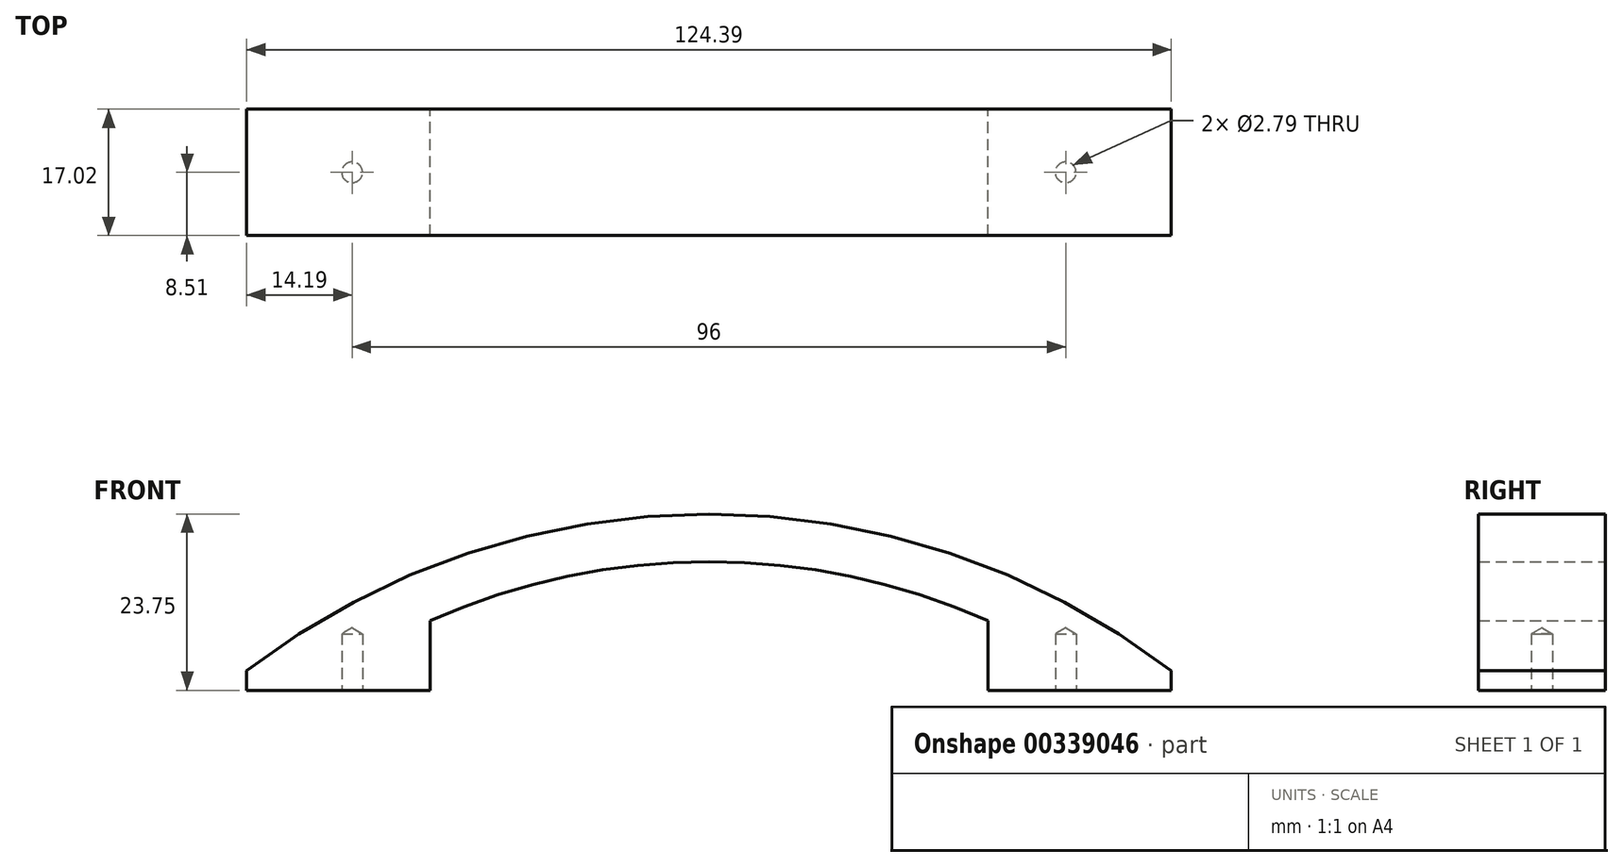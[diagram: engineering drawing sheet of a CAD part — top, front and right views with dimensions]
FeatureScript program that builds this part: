
annotation { "Feature Type Name" : "Feature", "Feature Type Description" : "" }
export const myFeature = defineFeature(function(context is Context, id is Id, definition is map)
    precondition{}
    {
        {
            var Q0;
            Q0=qCreatedBy(makeId("Front.planeOp"),FACE);
            var sketch = newSketch(context, id + "F0", { "sketchPlane" : qUnion([Q0])});
            skLineSegment(sketch, "E0", {"start": v(-68.67, -8.08) * mm, "end": v(-68.67, -10.75) * mm});
            skLineSegment(sketch, "E1", {"start": v(-68.67, -10.75) * mm, "end": v(-44, -10.75) * mm});
            skLineSegment(sketch, "E2", {"start": v(-44, -10.75) * mm, "end": v(-44, -1.36) * mm});
            skLineSegment(sketch, "E3", {"start": v(55.72, -8.08) * mm, "end": v(55.72, -10.75) * mm});
            skLineSegment(sketch, "E4", {"start": v(55.72, -10.75) * mm, "end": v(31.05, -10.75) * mm});
            skLineSegment(sketch, "E5", {"start": v(31.05, -1.36) * mm, "end": v(31.05, -10.75) * mm});
            skArc(sketch, "E6", {"start": v(31.05, -1.36) * mm, "mid": v(-6.47, 6.59) * mm, "end": v(-44, -1.36) * mm});
            skArc(sketch, "E7", {"start": v(55.72, -8.08) * mm, "mid": v(-6.47, 13) * mm, "end": v(-68.67, -8.08) * mm});
            skSolve(sketch);
        }
        {
            var Q0;
            Q0=qCreatedBy(makeId("Top.planeOp"),FACE);
            var sketch = newSketch(context, id + "F1", { "sketchPlane" : qUnion([Q0])});
            skCircle(sketch, "E8", {"center": v(-54.48, 0) * mm, "radius": 2.41 * mm});
            skCircle(sketch, "E9", {"center": v(41.52, 0) * mm, "radius": 2.4 * mm});
            skSolve(sketch);
        }
        {
            var Q0;
            Q0=makeQuery(id+"F0.imprint","IMPRINT",FACE,{"disambiguationData":[TD([[makeQuery(id+"F0.imprint","IMPRINT",EDGE,{"derivedFrom":sQuery(id+"F0.wireOp",EDGE,"E0")}),1.0]])]});
            extrude(context, id + "F2", {"entities" : qUnion([Q0]), "endBound" : BoundingType.SYMMETRIC, "depth" : 17.02 * mm});
        }
        {
            var Q0;
            Q0=makeQuery(id+"F2.opExtrude","SWEPT_BODY",BODY,{"disambiguationData":[OSD([sQuery(id+"F0.wireOp",EDGE,"E0"),sQuery(id+"F0.wireOp",EDGE,"E1"),sQuery(id+"F0.wireOp",EDGE,"E2"),sQuery(id+"F0.wireOp",EDGE,"5XAEyJnZ-LeuS-r8Om-Gh7R-BXXXRmB7yhHq"),sQuery(id+"F0.wireOp",EDGE,"JDMGs0dZ-B2UI-33di-LpgX-bAo0wkp94UCw"),sQuery(id+"F0.wireOp",EDGE,"xeET2ry0-x1wG-Vcxs-cHQk-ozSN2ffyht4o")])]});
            var Q1;
            Q1=makeQuery(id+"F2.opExtrude","SWEPT_BODY",BODY,{"disambiguationData":[OSD([sQuery(id+"FR6GUcAM7FEuFwb_91.1.F0.wireOp",EDGE,"E0"),sQuery(id+"FR6GUcAM7FEuFwb_91.1.F0.wireOp",EDGE,"E1"),sQuery(id+"FR6GUcAM7FEuFwb_91.1.F0.wireOp",EDGE,"E2"),sQuery(id+"FR6GUcAM7FEuFwb_91.1.F0.wireOp",EDGE,"5XAEyJnZ-LeuS-r8Om-Gh7R-BXXXRmB7yhHq"),sQuery(id+"FR6GUcAM7FEuFwb_91.1.F0.wireOp",EDGE,"JDMGs0dZ-B2UI-33di-LpgX-bAo0wkp94UCw"),sQuery(id+"FR6GUcAM7FEuFwb_91.1.F0.wireOp",EDGE,"xeET2ry0-x1wG-Vcxs-cHQk-ozSN2ffyht4o")])]});
            transform(context, id + "F3", {"entities" : qUnion([Q0, Q1]), "transformType" : TransformType.TRANSLATION_3D, "dx" : 0 * mm, "dy" : 0 * mm, "dz" : 10.82 * mm, "makeCopy" : false});
        }
        {
            var Q0;
            Q0=sQuery(id+"F1.wireOp",VERTEX,"E8.center");
            var Q1;
            Q1=sQuery(id+"F1.wireOp",VERTEX,"E9.center");
            var Q2;
            Q2=makeQuery(id+"F2.opExtrude","SWEPT_BODY",BODY,{"disambiguationData":[OSD([sQuery(id+"F0.wireOp",EDGE,"E0"),sQuery(id+"F0.wireOp",EDGE,"E1"),sQuery(id+"F0.wireOp",EDGE,"E2"),sQuery(id+"F0.wireOp",EDGE,"5XAEyJnZ-LeuS-r8Om-Gh7R-BXXXRmB7yhHq"),sQuery(id+"F0.wireOp",EDGE,"JDMGs0dZ-B2UI-33di-LpgX-bAo0wkp94UCw"),sQuery(id+"F0.wireOp",EDGE,"xeET2ry0-x1wG-Vcxs-cHQk-ozSN2ffyht4o")])]});
            hole(context, id + "F4", {"style" : HoleStyle.SIMPLE, "endStyle" : HoleEndStyle.BLIND, "oppositeDirection" : true, "holeDiameter" : 2.8 * mm, "holeDepth" : 7.62 * mm, "tappedDepth" : 12.7 * mm, "tapClearance" : 3, "locations" : qUnion([Q0, Q1]), "scope" : qUnion([Q2])});
        }
    });
